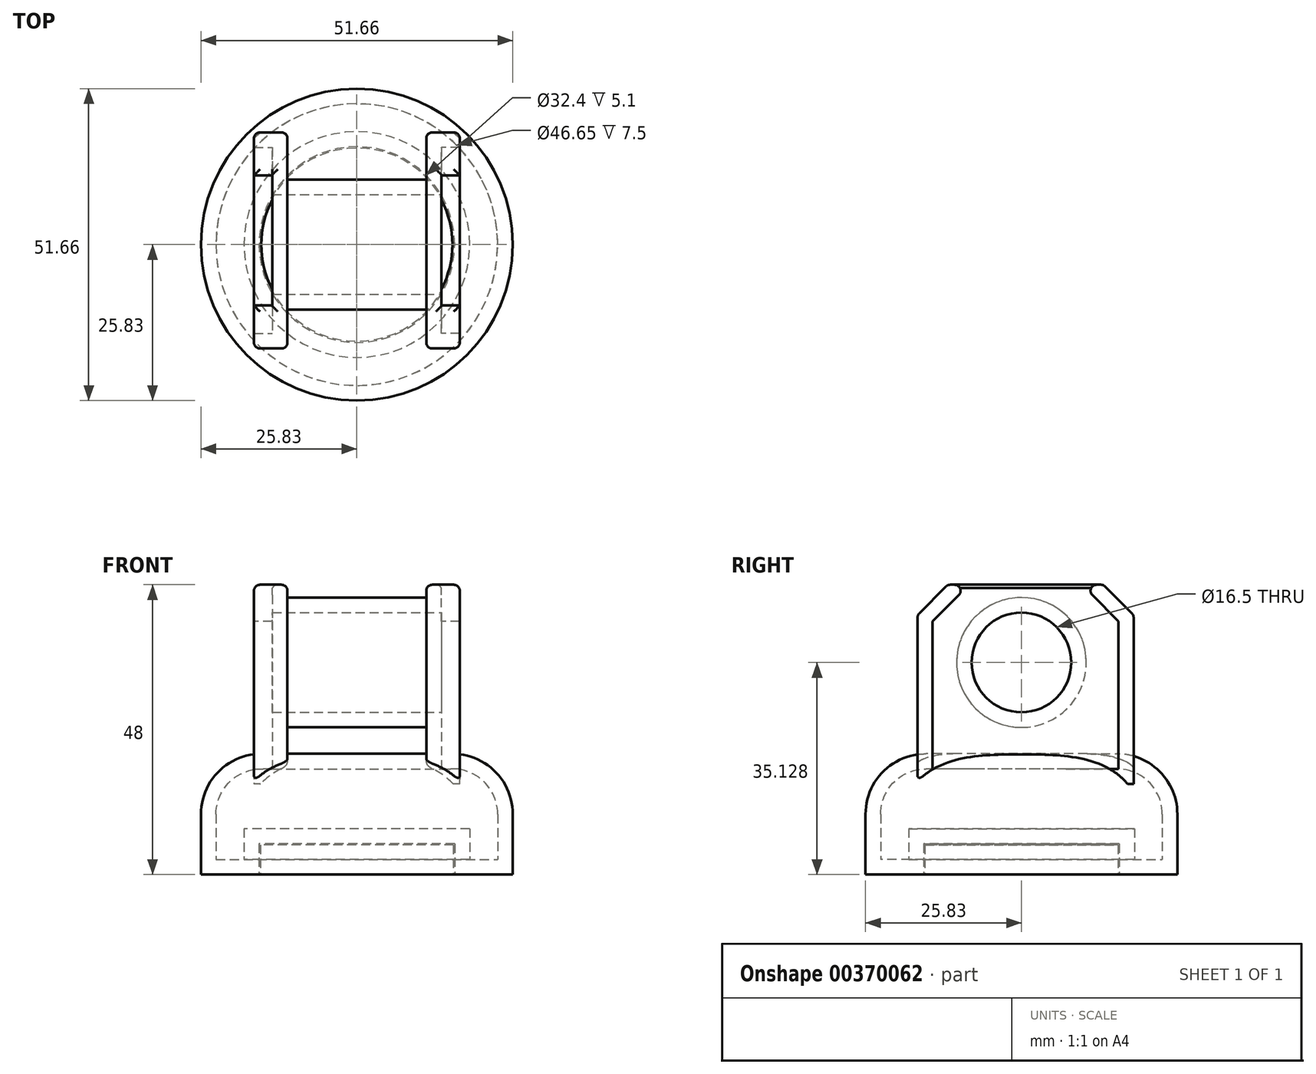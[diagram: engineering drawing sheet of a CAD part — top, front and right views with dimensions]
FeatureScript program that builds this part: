
annotation { "Feature Type Name" : "Feature", "Feature Type Description" : "" }
export const myFeature = defineFeature(function(context is Context, id is Id, definition is map)
    precondition{}
    {
        {
            var Q0;
            Q0=qCreatedBy(makeId("Top.planeOp"),FACE);
            var sketch = newSketch(context, id + "F0", { "sketchPlane" : qUnion([Q0])});
            skCircle(sketch, "E0", {"center": v(0, 0) * mm, "radius": 16 * mm});
            skSolve(sketch);
        }
        {
            var Q0;
            Q0 = qSketchRegion(id + "F0", true);
            extrude(context, id + "F1", {"entities" : qUnion([Q0]), "depth" : 4.9 * mm});
        }
        {
            var Q0;
            Q0=qCreatedBy(makeId("Top.planeOp"),FACE);
            var sketch = newSketch(context, id + "F2", { "sketchPlane" : qUnion([Q0])});
            skCircle(sketch, "E1", {"center": v(0, 0) * mm, "radius": 25.83 * mm});
            skSolve(sketch);
        }
        {
            var Q0;
            Q0 = qSketchRegion(id + "F2", true);
            extrude(context, id + "F3", {"entities" : qUnion([Q0]), "depth" : 20 * mm});
        }
        {
            var Q0;
            Q0=makeQuery(id+"F1.opExtrude","SWEPT_BODY",BODY,{"disambiguationData":[OSD([sQuery(id+"F0.wireOp",EDGE,"E0")])]});
            var Q1;
            Q1=makeQuery(id+"F3.opExtrude","SWEPT_BODY",BODY,{"disambiguationData":[OSD([sQuery(id+"F2.wireOp",EDGE,"E1")])]});
            booleanBodies(context, id + "F4", {"operationType" : BooleanOperationType.SUBTRACTION, "tools" : qUnion([Q0]), "targets" : qUnion([Q1]), "offset" : true, "offsetAll" : true, "offsetDistance" : 0.2 * mm, "keepTools" : true});
        }
        {
            var Q0;
            Q0=makeQuery(id+"F3.opExtrude","CAP_EDGE",EDGE,{"disambiguationData":[OSD([sQuery(id+"F2.wireOp",EDGE,"E1")])],"isStart":false});
            fillet(context, id + "F5", {"entities" : qUnion([Q0]), "radius" : 10 * mm, "tangentPropagation" : true, "allowEdgeOverflow" : false});
        }
        {
            var Q0;
            Q0=makeQuery(id+"F3.opExtrude","CAP_FACE",FACE,{"disambiguationData":[OSD([sQuery(id+"F2.wireOp",EDGE,"E1")])],"isStart":false});
            var sketch = newSketch(context, id + "F6", { "sketchPlane" : qUnion([Q0])});
            skLineSegment(sketch, "E2.bottom", {"start": v(-17.05, 18.58) * mm, "end": v(-11.5, 18.58) * mm});
            skLineSegment(sketch, "E2.top", {"start": v(-17.05, -17.2) * mm, "end": v(-11.5, -17.2) * mm});
            skLineSegment(sketch, "E2.left", {"start": v(-17.05, 18.58) * mm, "end": v(-17.05, -17.2) * mm});
            skLineSegment(sketch, "E2.right", {"start": v(-11.5, 18.58) * mm, "end": v(-11.5, -17.2) * mm});
            skSolve(sketch);
        }
        {
            var Q0;
            Q0 = qSketchRegion(id + "F6", true);
            extrude(context, id + "F7", {"entities" : qUnion([Q0]), "depth" : 28 * mm, "hasSecondDirection" : true, "secondDirectionOppositeDirection" : true, "secondDirectionDepth" : 5 * mm});
        }
        {
            var Q0;
            Q0=makeQuery(id+"F7.opExtrude","SWEPT_BODY",BODY,{"disambiguationData":[OSD([sQuery(id+"F6.wireOp",EDGE,"E2.bottom"),sQuery(id+"F6.wireOp",EDGE,"E2.top"),sQuery(id+"F6.wireOp",EDGE,"E2.left"),sQuery(id+"F6.wireOp",EDGE,"E2.right")])]});
            var Q1;
            Q1=qCreatedBy(makeId("Right.planeOp"),FACE);
            mirror(context, id + "F8", {"operationType" : NewBodyOperationType.ADD, "entities" : qUnion([Q0]), "mirrorPlane" : qUnion([Q1])});
        }
        {
            var Q0;
            Q0=makeQuery(id+"F8.opPattern","COPY",FACE,{"derivedFrom":makeQuery(id+"F7.opExtrude","SWEPT_FACE",FACE,{"disambiguationData":[OSD([sQuery(id+"F6.wireOp",EDGE,"E2.left")])]}),"instanceName":"1"});
            var sketch = newSketch(context, id + "F9", { "sketchPlane" : qUnion([Q0])});
            skCircle(sketch, "E3", {"center": v(0, 35.13) * mm, "radius": 10.75 * mm});
            skSolve(sketch);
        }
        {
            var Q0;
            Q0 = qSketchRegion(id + "F9", true);
            var Q1;
            Q1=makeQuery(id+"F7.opExtrude","SWEPT_FACE",FACE,{"disambiguationData":[OSD([sQuery(id+"F6.wireOp",EDGE,"E2.right")])]});
            extrude(context, id + "F10", {"entities" : qUnion([Q0]), "operationType" : NewBodyOperationType.ADD, "endBound" : BoundingType.UP_TO_SURFACE, "oppositeDirection" : true, "endBoundEntityFace" : qUnion([Q1]), "depth" : 25 * mm});
        }
        {
            var Q0;
            Q0=makeQuery(id+"F7.opExtrude","CAP_EDGE",EDGE,{"disambiguationData":[OSD([sQuery(id+"F6.wireOp",EDGE,"E2.top")])],"isStart":false});
            var Q1;
            Q1=makeQuery(id+"F7.opExtrude","CAP_EDGE",EDGE,{"disambiguationData":[OSD([sQuery(id+"F6.wireOp",EDGE,"E2.bottom")])],"isStart":false});
            var Q2;
            Q2=makeQuery(id+"F8.opPattern","COPY",EDGE,{"derivedFrom":makeQuery(id+"F7.opExtrude","CAP_EDGE",EDGE,{"disambiguationData":[OSD([sQuery(id+"F6.wireOp",EDGE,"E2.bottom")])],"isStart":false}),"instanceName":"1"});
            var Q3;
            Q3=makeQuery(id+"F8.opPattern","COPY",EDGE,{"derivedFrom":makeQuery(id+"F7.opExtrude","CAP_EDGE",EDGE,{"disambiguationData":[OSD([sQuery(id+"F6.wireOp",EDGE,"E2.top")])],"isStart":false}),"instanceName":"1"});
            chamfer(context, id + "F11", {"entities" : qUnion([Q0, Q1, Q2, Q3]), "width" : 5 * mm, "tangentPropagation" : true});
        }
        {
            var Q0;
            Q0=makeQuery(id+"F8.opPattern","COPY",FACE,{"derivedFrom":makeQuery(id+"F7.opExtrude","SWEPT_FACE",FACE,{"disambiguationData":[OSD([sQuery(id+"F6.wireOp",EDGE,"E2.left")])]}),"instanceName":"1"});
            var Q1;
            Q1=makeQuery(id+"F7.opExtrude","SWEPT_FACE",FACE,{"disambiguationData":[OSD([sQuery(id+"F6.wireOp",EDGE,"E2.left")])]});
            shell(context, id + "F12", {"entities" : qUnion([Q0, Q1]), "thickness" : 2.5 * mm});
        }
        {
            var Q0;
            {var subQ0=sQuery(id+"F6.wireOp",EDGE,"E2.left");Q0=makeQuery(id+"F12.opShell","OFFSET_EDGE",EDGE,{"disambiguationData":[OSD([subQ0]),TDD([makeQuery(id+"F8.opPattern","COPY",EDGE,{"derivedFrom":makeQuery(id+"F7.opExtrude","CAP_EDGE",EDGE,{"disambiguationData":[OSD([subQ0])],"isStart":false}),"instanceName":"1"})])]});}
            var Q1;
            {var subQ0=sQuery(id+"F6.wireOp",EDGE,"E2.left");Q1=makeQuery(id+"F12.opShell","OFFSET_EDGE",EDGE,{"disambiguationData":[OSD([subQ0]),TDD([makeQuery(id+"F7.opExtrude","CAP_EDGE",EDGE,{"disambiguationData":[OSD([subQ0])],"isStart":false})])]});}
            chamfer(context, id + "F13", {"entities" : qUnion([Q0, Q1]), "width" : 5 * mm, "tangentPropagation" : true});
        }
        {
            var Q0;
            Q0=makeQuery(id+"F7.opExtrude","SWEPT_EDGE",EDGE,{"disambiguationData":[OSD([sQuery(id+"F6.wireOp",EDGE,"E2.top"),sQuery(id+"F6.wireOp",EDGE,"E2.left")])]});
            var Q1;
            Q1=makeQuery(id+"F11.opChamfer","BLEND_EDGE",EDGE,{"blendedFrom":[makeQuery(id+"F7.opExtrude","CAP_EDGE",EDGE,{"disambiguationData":[OSD([sQuery(id+"F6.wireOp",EDGE,"E2.top")])],"isStart":false}),makeQuery(id+"F7.opExtrude","SWEPT_FACE",FACE,{"disambiguationData":[OSD([sQuery(id+"F6.wireOp",EDGE,"E2.left")])]})],"blendedInto":[makeQuery(id+"F7.opExtrude","SWEPT_FACE",FACE,{"disambiguationData":[OSD([sQuery(id+"F6.wireOp",EDGE,"E2.left")])]})]});
            var Q2;
            {var subQ0=sQuery(id+"F6.wireOp",EDGE,"E2.top");Q2=makeQuery(id+"F11.opChamfer","BLEND_EDGE",EDGE,{"blendedFrom":[makeQuery(id+"F7.opExtrude","CAP_EDGE",EDGE,{"disambiguationData":[OSD([subQ0])],"isStart":false}),makeQuery(id+"F7.opExtrude","CAP_FACE",FACE,{"disambiguationData":[OSD([sQuery(id+"F6.wireOp",EDGE,"E2.bottom"),subQ0,sQuery(id+"F6.wireOp",EDGE,"E2.left"),sQuery(id+"F6.wireOp",EDGE,"E2.right")])],"isStart":false})],"blendedInto":[makeQuery(id+"F7.opExtrude","CAP_FACE",FACE,{"disambiguationData":[OSD([sQuery(id+"F6.wireOp",EDGE,"E2.bottom"),subQ0,sQuery(id+"F6.wireOp",EDGE,"E2.left"),sQuery(id+"F6.wireOp",EDGE,"E2.right")])],"isStart":false})]});}
            var Q3;
            Q3=makeQuery(id+"F11.opChamfer","BLEND_EDGE",EDGE,{"blendedFrom":[makeQuery(id+"F7.opExtrude","CAP_EDGE",EDGE,{"disambiguationData":[OSD([sQuery(id+"F6.wireOp",EDGE,"E2.top")])],"isStart":false}),makeQuery(id+"F7.opExtrude","SWEPT_FACE",FACE,{"disambiguationData":[OSD([sQuery(id+"F6.wireOp",EDGE,"E2.right")])]})],"blendedInto":[makeQuery(id+"F7.opExtrude","SWEPT_FACE",FACE,{"disambiguationData":[OSD([sQuery(id+"F6.wireOp",EDGE,"E2.right")])]})]});
            var Q4;
            Q4=makeQuery(id+"F7.opExtrude","SWEPT_EDGE",EDGE,{"disambiguationData":[OSD([sQuery(id+"F6.wireOp",EDGE,"E2.top"),sQuery(id+"F6.wireOp",EDGE,"E2.right")])]});
            var Q5;
            Q5=makeQuery(id+"F8.opPattern","COPY",EDGE,{"derivedFrom":makeQuery(id+"F7.opExtrude","SWEPT_EDGE",EDGE,{"disambiguationData":[OSD([sQuery(id+"F6.wireOp",EDGE,"E2.top"),sQuery(id+"F6.wireOp",EDGE,"E2.right")])]}),"instanceName":"1"});
            var Q6;
            Q6=makeQuery(id+"F11.opChamfer","BLEND_EDGE",EDGE,{"blendedFrom":[makeQuery(id+"F8.opPattern","COPY",EDGE,{"derivedFrom":makeQuery(id+"F7.opExtrude","CAP_EDGE",EDGE,{"disambiguationData":[OSD([sQuery(id+"F6.wireOp",EDGE,"E2.top")])],"isStart":false}),"instanceName":"1"}),makeQuery(id+"F8.opPattern","COPY",FACE,{"derivedFrom":makeQuery(id+"F7.opExtrude","SWEPT_FACE",FACE,{"disambiguationData":[OSD([sQuery(id+"F6.wireOp",EDGE,"E2.right")])]}),"instanceName":"1"})],"blendedInto":[makeQuery(id+"F8.opPattern","COPY",FACE,{"derivedFrom":makeQuery(id+"F7.opExtrude","SWEPT_FACE",FACE,{"disambiguationData":[OSD([sQuery(id+"F6.wireOp",EDGE,"E2.right")])]}),"instanceName":"1"})]});
            var Q7;
            {var subQ0=sQuery(id+"F6.wireOp",EDGE,"E2.top");Q7=makeQuery(id+"F11.opChamfer","BLEND_EDGE",EDGE,{"blendedFrom":[makeQuery(id+"F8.opPattern","COPY",EDGE,{"derivedFrom":makeQuery(id+"F7.opExtrude","CAP_EDGE",EDGE,{"disambiguationData":[OSD([subQ0])],"isStart":false}),"instanceName":"1"}),makeQuery(id+"F8.opPattern","COPY",FACE,{"derivedFrom":makeQuery(id+"F7.opExtrude","CAP_FACE",FACE,{"disambiguationData":[OSD([sQuery(id+"F6.wireOp",EDGE,"E2.bottom"),subQ0,sQuery(id+"F6.wireOp",EDGE,"E2.left"),sQuery(id+"F6.wireOp",EDGE,"E2.right")])],"isStart":false}),"instanceName":"1"})],"blendedInto":[makeQuery(id+"F8.opPattern","COPY",FACE,{"derivedFrom":makeQuery(id+"F7.opExtrude","CAP_FACE",FACE,{"disambiguationData":[OSD([sQuery(id+"F6.wireOp",EDGE,"E2.bottom"),subQ0,sQuery(id+"F6.wireOp",EDGE,"E2.left"),sQuery(id+"F6.wireOp",EDGE,"E2.right")])],"isStart":false}),"instanceName":"1"})]});}
            var Q8;
            Q8=makeQuery(id+"F11.opChamfer","BLEND_EDGE",EDGE,{"blendedFrom":[makeQuery(id+"F8.opPattern","COPY",EDGE,{"derivedFrom":makeQuery(id+"F7.opExtrude","CAP_EDGE",EDGE,{"disambiguationData":[OSD([sQuery(id+"F6.wireOp",EDGE,"E2.top")])],"isStart":false}),"instanceName":"1"}),makeQuery(id+"F8.opPattern","COPY",FACE,{"derivedFrom":makeQuery(id+"F7.opExtrude","SWEPT_FACE",FACE,{"disambiguationData":[OSD([sQuery(id+"F6.wireOp",EDGE,"E2.left")])]}),"instanceName":"1"})],"blendedInto":[makeQuery(id+"F8.opPattern","COPY",FACE,{"derivedFrom":makeQuery(id+"F7.opExtrude","SWEPT_FACE",FACE,{"disambiguationData":[OSD([sQuery(id+"F6.wireOp",EDGE,"E2.left")])]}),"instanceName":"1"})]});
            var Q9;
            Q9=makeQuery(id+"F8.opPattern","COPY",EDGE,{"derivedFrom":makeQuery(id+"F7.opExtrude","SWEPT_EDGE",EDGE,{"disambiguationData":[OSD([sQuery(id+"F6.wireOp",EDGE,"E2.top"),sQuery(id+"F6.wireOp",EDGE,"E2.left")])]}),"instanceName":"1"});
            var Q10;
            Q10=makeQuery(id+"F8.opPattern","COPY",EDGE,{"derivedFrom":makeQuery(id+"F7.opExtrude","SWEPT_EDGE",EDGE,{"disambiguationData":[OSD([sQuery(id+"F6.wireOp",EDGE,"E2.bottom"),sQuery(id+"F6.wireOp",EDGE,"E2.left")])]}),"instanceName":"1"});
            var Q11;
            Q11=makeQuery(id+"F8.opPattern","COPY",EDGE,{"derivedFrom":makeQuery(id+"F7.opExtrude","SWEPT_EDGE",EDGE,{"disambiguationData":[OSD([sQuery(id+"F6.wireOp",EDGE,"E2.bottom"),sQuery(id+"F6.wireOp",EDGE,"E2.right")])]}),"instanceName":"1"});
            var Q12;
            Q12=makeQuery(id+"F11.opChamfer","BLEND_EDGE",EDGE,{"blendedFrom":[makeQuery(id+"F8.opPattern","COPY",EDGE,{"derivedFrom":makeQuery(id+"F7.opExtrude","CAP_EDGE",EDGE,{"disambiguationData":[OSD([sQuery(id+"F6.wireOp",EDGE,"E2.bottom")])],"isStart":false}),"instanceName":"1"}),makeQuery(id+"F8.opPattern","COPY",FACE,{"derivedFrom":makeQuery(id+"F7.opExtrude","SWEPT_FACE",FACE,{"disambiguationData":[OSD([sQuery(id+"F6.wireOp",EDGE,"E2.left")])]}),"instanceName":"1"})],"blendedInto":[makeQuery(id+"F8.opPattern","COPY",FACE,{"derivedFrom":makeQuery(id+"F7.opExtrude","SWEPT_FACE",FACE,{"disambiguationData":[OSD([sQuery(id+"F6.wireOp",EDGE,"E2.left")])]}),"instanceName":"1"})]});
            var Q13;
            Q13=makeQuery(id+"F11.opChamfer","BLEND_EDGE",EDGE,{"blendedFrom":[makeQuery(id+"F8.opPattern","COPY",EDGE,{"derivedFrom":makeQuery(id+"F7.opExtrude","CAP_EDGE",EDGE,{"disambiguationData":[OSD([sQuery(id+"F6.wireOp",EDGE,"E2.bottom")])],"isStart":false}),"instanceName":"1"}),makeQuery(id+"F8.opPattern","COPY",FACE,{"derivedFrom":makeQuery(id+"F7.opExtrude","SWEPT_FACE",FACE,{"disambiguationData":[OSD([sQuery(id+"F6.wireOp",EDGE,"E2.right")])]}),"instanceName":"1"})],"blendedInto":[makeQuery(id+"F8.opPattern","COPY",FACE,{"derivedFrom":makeQuery(id+"F7.opExtrude","SWEPT_FACE",FACE,{"disambiguationData":[OSD([sQuery(id+"F6.wireOp",EDGE,"E2.right")])]}),"instanceName":"1"})]});
            var Q14;
            {var subQ0=sQuery(id+"F6.wireOp",EDGE,"E2.bottom");Q14=makeQuery(id+"F11.opChamfer","BLEND_EDGE",EDGE,{"blendedFrom":[makeQuery(id+"F8.opPattern","COPY",EDGE,{"derivedFrom":makeQuery(id+"F7.opExtrude","CAP_EDGE",EDGE,{"disambiguationData":[OSD([subQ0])],"isStart":false}),"instanceName":"1"}),makeQuery(id+"F8.opPattern","COPY",FACE,{"derivedFrom":makeQuery(id+"F7.opExtrude","CAP_FACE",FACE,{"disambiguationData":[OSD([subQ0,sQuery(id+"F6.wireOp",EDGE,"E2.top"),sQuery(id+"F6.wireOp",EDGE,"E2.left"),sQuery(id+"F6.wireOp",EDGE,"E2.right")])],"isStart":false}),"instanceName":"1"})],"blendedInto":[makeQuery(id+"F8.opPattern","COPY",FACE,{"derivedFrom":makeQuery(id+"F7.opExtrude","CAP_FACE",FACE,{"disambiguationData":[OSD([subQ0,sQuery(id+"F6.wireOp",EDGE,"E2.top"),sQuery(id+"F6.wireOp",EDGE,"E2.left"),sQuery(id+"F6.wireOp",EDGE,"E2.right")])],"isStart":false}),"instanceName":"1"})]});}
            var Q15;
            Q15=makeQuery(id+"F7.opExtrude","SWEPT_EDGE",EDGE,{"disambiguationData":[OSD([sQuery(id+"F6.wireOp",EDGE,"E2.bottom"),sQuery(id+"F6.wireOp",EDGE,"E2.right")])]});
            var Q16;
            Q16=makeQuery(id+"F11.opChamfer","BLEND_EDGE",EDGE,{"blendedFrom":[makeQuery(id+"F7.opExtrude","CAP_EDGE",EDGE,{"disambiguationData":[OSD([sQuery(id+"F6.wireOp",EDGE,"E2.bottom")])],"isStart":false}),makeQuery(id+"F7.opExtrude","SWEPT_FACE",FACE,{"disambiguationData":[OSD([sQuery(id+"F6.wireOp",EDGE,"E2.right")])]})],"blendedInto":[makeQuery(id+"F7.opExtrude","SWEPT_FACE",FACE,{"disambiguationData":[OSD([sQuery(id+"F6.wireOp",EDGE,"E2.right")])]})]});
            var Q17;
            Q17=makeQuery(id+"F11.opChamfer","BLEND_EDGE",EDGE,{"blendedFrom":[makeQuery(id+"F7.opExtrude","CAP_EDGE",EDGE,{"disambiguationData":[OSD([sQuery(id+"F6.wireOp",EDGE,"E2.bottom")])],"isStart":false}),makeQuery(id+"F7.opExtrude","SWEPT_FACE",FACE,{"disambiguationData":[OSD([sQuery(id+"F6.wireOp",EDGE,"E2.left")])]})],"blendedInto":[makeQuery(id+"F7.opExtrude","SWEPT_FACE",FACE,{"disambiguationData":[OSD([sQuery(id+"F6.wireOp",EDGE,"E2.left")])]})]});
            var Q18;
            Q18=makeQuery(id+"F7.opExtrude","SWEPT_EDGE",EDGE,{"disambiguationData":[OSD([sQuery(id+"F6.wireOp",EDGE,"E2.bottom"),sQuery(id+"F6.wireOp",EDGE,"E2.left")])]});
            var Q19;
            {var subQ0=sQuery(id+"F6.wireOp",EDGE,"E2.bottom");Q19=makeQuery(id+"F11.opChamfer","BLEND_EDGE",EDGE,{"blendedFrom":[makeQuery(id+"F7.opExtrude","CAP_EDGE",EDGE,{"disambiguationData":[OSD([subQ0])],"isStart":false}),makeQuery(id+"F7.opExtrude","SWEPT_FACE",FACE,{"disambiguationData":[OSD([subQ0])]})],"blendedInto":[makeQuery(id+"F7.opExtrude","SWEPT_FACE",FACE,{"disambiguationData":[OSD([subQ0])]})]});}
            var Q20;
            {var subQ0=sQuery(id+"F6.wireOp",EDGE,"E2.bottom");Q20=makeQuery(id+"F11.opChamfer","BLEND_EDGE",EDGE,{"blendedFrom":[makeQuery(id+"F7.opExtrude","CAP_EDGE",EDGE,{"disambiguationData":[OSD([subQ0])],"isStart":false}),makeQuery(id+"F7.opExtrude","CAP_FACE",FACE,{"disambiguationData":[OSD([subQ0,sQuery(id+"F6.wireOp",EDGE,"E2.top"),sQuery(id+"F6.wireOp",EDGE,"E2.left"),sQuery(id+"F6.wireOp",EDGE,"E2.right")])],"isStart":false})],"blendedInto":[makeQuery(id+"F7.opExtrude","CAP_FACE",FACE,{"disambiguationData":[OSD([subQ0,sQuery(id+"F6.wireOp",EDGE,"E2.top"),sQuery(id+"F6.wireOp",EDGE,"E2.left"),sQuery(id+"F6.wireOp",EDGE,"E2.right")])],"isStart":false})]});}
            var Q21;
            {var subQ0=sQuery(id+"F6.wireOp",EDGE,"E2.bottom");Q21=makeQuery(id+"F11.opChamfer","BLEND_EDGE",EDGE,{"blendedFrom":[makeQuery(id+"F8.opPattern","COPY",EDGE,{"derivedFrom":makeQuery(id+"F7.opExtrude","CAP_EDGE",EDGE,{"disambiguationData":[OSD([subQ0])],"isStart":false}),"instanceName":"1"}),makeQuery(id+"F8.opPattern","COPY",FACE,{"derivedFrom":makeQuery(id+"F7.opExtrude","SWEPT_FACE",FACE,{"disambiguationData":[OSD([subQ0])]}),"instanceName":"1"})],"blendedInto":[makeQuery(id+"F8.opPattern","COPY",FACE,{"derivedFrom":makeQuery(id+"F7.opExtrude","SWEPT_FACE",FACE,{"disambiguationData":[OSD([subQ0])]}),"instanceName":"1"})]});}
            var Q22;
            {var subQ0=sQuery(id+"F6.wireOp",EDGE,"E2.top");Q22=makeQuery(id+"F11.opChamfer","BLEND_EDGE",EDGE,{"blendedFrom":[makeQuery(id+"F8.opPattern","COPY",EDGE,{"derivedFrom":makeQuery(id+"F7.opExtrude","CAP_EDGE",EDGE,{"disambiguationData":[OSD([subQ0])],"isStart":false}),"instanceName":"1"}),makeQuery(id+"F8.opPattern","COPY",FACE,{"derivedFrom":makeQuery(id+"F7.opExtrude","SWEPT_FACE",FACE,{"disambiguationData":[OSD([subQ0])]}),"instanceName":"1"})],"blendedInto":[makeQuery(id+"F8.opPattern","COPY",FACE,{"derivedFrom":makeQuery(id+"F7.opExtrude","SWEPT_FACE",FACE,{"disambiguationData":[OSD([subQ0])]}),"instanceName":"1"})]});}
            var Q23;
            {var subQ0=sQuery(id+"F6.wireOp",EDGE,"E2.top");Q23=makeQuery(id+"F11.opChamfer","BLEND_EDGE",EDGE,{"blendedFrom":[makeQuery(id+"F7.opExtrude","CAP_EDGE",EDGE,{"disambiguationData":[OSD([subQ0])],"isStart":false}),makeQuery(id+"F7.opExtrude","SWEPT_FACE",FACE,{"disambiguationData":[OSD([subQ0])]})],"blendedInto":[makeQuery(id+"F7.opExtrude","SWEPT_FACE",FACE,{"disambiguationData":[OSD([subQ0])]})]});}
            var Q24;
            Q24=makeQuery(id+"F8.opPattern","COPY",EDGE,{"derivedFrom":makeQuery(id+"F7.opExtrude","CAP_EDGE",EDGE,{"disambiguationData":[OSD([sQuery(id+"F6.wireOp",EDGE,"E2.right")])],"isStart":false}),"instanceName":"1"});
            var Q25;
            Q25=makeQuery(id+"F7.opExtrude","CAP_FACE",FACE,{"disambiguationData":[OSD([sQuery(id+"F6.wireOp",EDGE,"E2.bottom"),sQuery(id+"F6.wireOp",EDGE,"E2.top"),sQuery(id+"F6.wireOp",EDGE,"E2.left"),sQuery(id+"F6.wireOp",EDGE,"E2.right")])],"isStart":false});
            var Q26;
            {var subQ0=sQuery(id+"F6.wireOp",EDGE,"E2.left");Q26=makeQuery(id+"F13.opChamfer","BLEND_EDGE",EDGE,{"blendedFrom":[makeQuery(id+"F12.opShell","OFFSET_EDGE",EDGE,{"disambiguationData":[OSD([subQ0]),TDD([makeQuery(id+"F8.opPattern","COPY",EDGE,{"derivedFrom":makeQuery(id+"F7.opExtrude","CAP_EDGE",EDGE,{"disambiguationData":[OSD([subQ0])],"isStart":false}),"instanceName":"1"})])]}),makeQuery(id+"F8.opPattern","COPY",FACE,{"derivedFrom":makeQuery(id+"F7.opExtrude","CAP_FACE",FACE,{"disambiguationData":[OSD([sQuery(id+"F6.wireOp",EDGE,"E2.bottom"),sQuery(id+"F6.wireOp",EDGE,"E2.top"),subQ0,sQuery(id+"F6.wireOp",EDGE,"E2.right")])],"isStart":false}),"instanceName":"1"})],"blendedInto":[makeQuery(id+"F8.opPattern","COPY",FACE,{"derivedFrom":makeQuery(id+"F7.opExtrude","CAP_FACE",FACE,{"disambiguationData":[OSD([sQuery(id+"F6.wireOp",EDGE,"E2.bottom"),sQuery(id+"F6.wireOp",EDGE,"E2.top"),subQ0,sQuery(id+"F6.wireOp",EDGE,"E2.right")])],"isStart":false}),"instanceName":"1"})]});}
            var Q27;
            Q27=makeQuery(id+"F8.opPattern","COPY",EDGE,{"derivedFrom":makeQuery(id+"F7.opExtrude","CAP_EDGE",EDGE,{"disambiguationData":[OSD([sQuery(id+"F6.wireOp",EDGE,"E2.left")])],"isStart":false}),"instanceName":"1"});
            var Q28;
            {var subQ0=sQuery(id+"F6.wireOp",EDGE,"E2.left");var subQ1=sQuery(id+"F6.wireOp",EDGE,"E2.right");var subQ2=sQuery(id+"F6.wireOp",EDGE,"E2.top");var subQ3=sQuery(id+"F6.wireOp",EDGE,"E2.bottom");Q28=makeQuery(id+"F13.opChamfer","TWEAK_EDGE",EDGE,{"derivedFrom":[makeQuery(id+"F12.opShell","OFFSET_VERTEX",VERTEX,{"disambiguationData":[OSD([subQ3,subQ2,subQ0,subQ1]),TDD([makeQuery(id+"F11.opChamfer","BLEND_VERTEX",VERTEX,{"blendedFrom":[makeQuery(id+"F8.opPattern","COPY",EDGE,{"derivedFrom":makeQuery(id+"F7.opExtrude","CAP_EDGE",EDGE,{"disambiguationData":[OSD([subQ2])],"isStart":false}),"instanceName":"1"}),makeQuery(id+"F8.opPattern","COPY",FACE,{"derivedFrom":makeQuery(id+"F7.opExtrude","CAP_FACE",FACE,{"disambiguationData":[OSD([subQ3,subQ2,subQ0,subQ1])],"isStart":false}),"instanceName":"1"}),makeQuery(id+"F8.opPattern","COPY",FACE,{"derivedFrom":makeQuery(id+"F7.opExtrude","SWEPT_FACE",FACE,{"disambiguationData":[OSD([subQ0])]}),"instanceName":"1"})],"blendedInto":[makeQuery(id+"F8.opPattern","COPY",FACE,{"derivedFrom":makeQuery(id+"F7.opExtrude","CAP_FACE",FACE,{"disambiguationData":[OSD([subQ3,subQ2,subQ0,subQ1])],"isStart":false}),"instanceName":"1"}),makeQuery(id+"F8.opPattern","COPY",FACE,{"derivedFrom":makeQuery(id+"F7.opExtrude","SWEPT_FACE",FACE,{"disambiguationData":[OSD([subQ0])]}),"instanceName":"1"})]})])]})]});}
            var Q29;
            {var subQ0=sQuery(id+"F6.wireOp",EDGE,"E2.left");var subQ1=sQuery(id+"F6.wireOp",EDGE,"E2.right");var subQ2=sQuery(id+"F6.wireOp",EDGE,"E2.top");var subQ3=sQuery(id+"F6.wireOp",EDGE,"E2.bottom");Q29=makeQuery(id+"F13.opChamfer","TWEAK_EDGE",EDGE,{"derivedFrom":[makeQuery(id+"F12.opShell","OFFSET_VERTEX",VERTEX,{"disambiguationData":[OSD([subQ3,subQ2,subQ0,subQ1]),TDD([makeQuery(id+"F11.opChamfer","BLEND_VERTEX",VERTEX,{"blendedFrom":[makeQuery(id+"F8.opPattern","COPY",EDGE,{"derivedFrom":makeQuery(id+"F7.opExtrude","CAP_EDGE",EDGE,{"disambiguationData":[OSD([subQ3])],"isStart":false}),"instanceName":"1"}),makeQuery(id+"F8.opPattern","COPY",FACE,{"derivedFrom":makeQuery(id+"F7.opExtrude","CAP_FACE",FACE,{"disambiguationData":[OSD([subQ3,subQ2,subQ0,subQ1])],"isStart":false}),"instanceName":"1"}),makeQuery(id+"F8.opPattern","COPY",FACE,{"derivedFrom":makeQuery(id+"F7.opExtrude","SWEPT_FACE",FACE,{"disambiguationData":[OSD([subQ0])]}),"instanceName":"1"})],"blendedInto":[makeQuery(id+"F8.opPattern","COPY",FACE,{"derivedFrom":makeQuery(id+"F7.opExtrude","CAP_FACE",FACE,{"disambiguationData":[OSD([subQ3,subQ2,subQ0,subQ1])],"isStart":false}),"instanceName":"1"}),makeQuery(id+"F8.opPattern","COPY",FACE,{"derivedFrom":makeQuery(id+"F7.opExtrude","SWEPT_FACE",FACE,{"disambiguationData":[OSD([subQ0])]}),"instanceName":"1"})]})])]})]});}
            fillet(context, id + "F14", {"entities" : qUnion([Q0, Q1, Q2, Q3, Q4, Q5, Q6, Q7, Q8, Q9, Q10, Q11, Q12, Q13, Q14, Q15, Q16, Q17, Q18, Q19, Q20, Q21, Q22, Q23, Q24, Q25, Q26, Q27, Q28, Q29]), "radius" : 1 * mm, "tangentPropagation" : true, "allowEdgeOverflow" : false});
        }
    });
